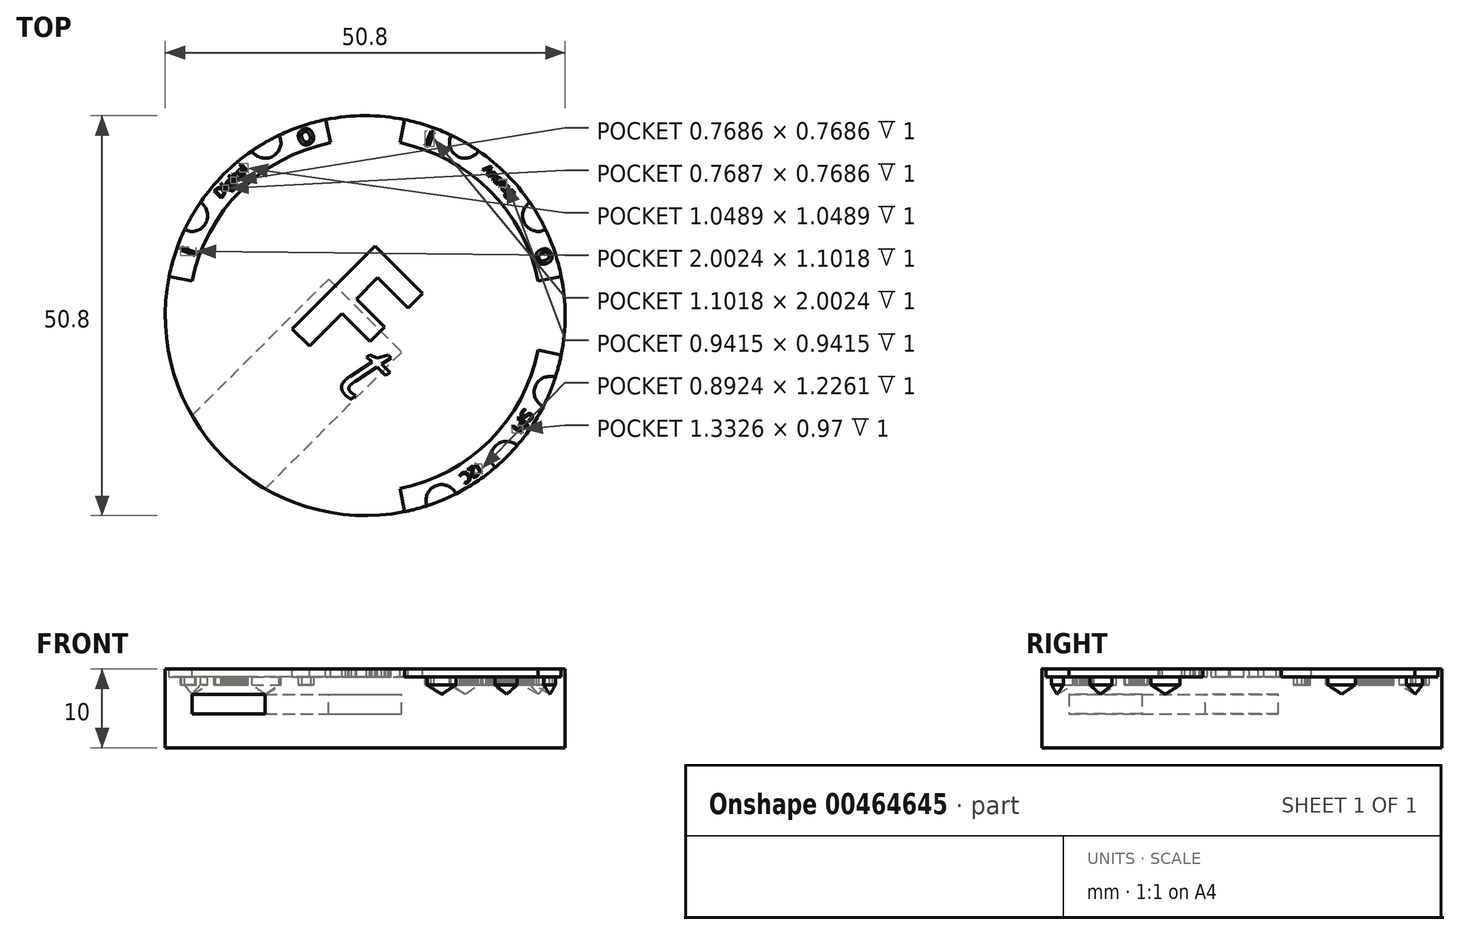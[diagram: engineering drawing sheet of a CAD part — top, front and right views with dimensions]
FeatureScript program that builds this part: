
annotation { "Feature Type Name" : "Feature", "Feature Type Description" : "" }
export const myFeature = defineFeature(function(context is Context, id is Id, definition is map)
    precondition{}
    {
        {
            var Q0;
            Q0=qCreatedBy(makeId("Top.planeOp"),FACE);
            var sketch = newSketch(context, id + "F0", { "sketchPlane" : qUnion([Q0])});
            skCircle(sketch, "E0", {"center": v(0, 0) * mm, "radius": 25.4 * mm});
            skSolve(sketch);
        }
        {
            var Q0;
            Q0=makeQuery(id+"F0.imprint","IMPRINT",FACE,{"disambiguationData":[TD([[makeQuery(id+"F0.imprint","IMPRINT",EDGE,{"derivedFrom":sQuery(id+"F0.wireOp",EDGE,"E0")}),1.0]])]});
            extrude(context, id + "F1", {"entities" : qUnion([Q0]), "depth" : 10 * mm});
        }
        {
            var Q0;
            Q0=makeQuery(id+"F1.opExtrude","CAP_FACE",FACE,{"disambiguationData":[OSD([sQuery(id+"F0.wireOp",EDGE,"E0")])],"isStart":false});
            var sketch = newSketch(context, id + "F2", { "sketchPlane" : qUnion([Q0])});
            skLineSegment(sketch, "E1", {"start": v(0, 0) * mm, "end": v(12.7, 22) * mm});
            skLineSegment(sketch, "E2", {"start": v(0, 0) * mm, "end": v(22, 12.7) * mm});
            skLineSegment(sketch, "E3", {"start": v(0, 25.4) * mm, "end": v(0, -25.4) * mm});
            skLineSegment(sketch, "E4", {"start": v(-25.4, 0) * mm, "end": v(25.4, 0) * mm});
            skLineSegment(sketch, "E5", {"start": v(0, 0) * mm, "end": v(-12.7, 22) * mm});
            skLineSegment(sketch, "E6", {"start": v(0, 0) * mm, "end": v(23.47, -9.72) * mm});
            skLineSegment(sketch, "E7", {"start": v(0, 0) * mm, "end": v(17.96, -17.96) * mm});
            skLineSegment(sketch, "E8", {"start": v(0, 0) * mm, "end": v(9.72, -23.47) * mm});
            skLineSegment(sketch, "E9", {"start": v(0, 0) * mm, "end": v(-17.96, -17.96) * mm});
            skLineSegment(sketch, "E10", {"start": v(0, 0) * mm, "end": v(-22, 12.7) * mm});
            skSolve(sketch);
        }
        {
            var Q0;
            Q0=sQuery(id+"F2.wireOp",VERTEX,"cUKKlthW-F4cE-I2rY-EU5q-HDzWbLOjQpO6.end");
            var Q1;
            Q1=sQuery(id+"F2.wireOp",VERTEX,"E5.end");
            var Q2;
            Q2=sQuery(id+"F2.wireOp",VERTEX,"E1.end");
            var Q3;
            Q3=sQuery(id+"F2.wireOp",VERTEX,"E2.end");
            var Q4;
            Q4=sQuery(id+"F2.wireOp",VERTEX,"E6.end");
            var Q5;
            Q5=sQuery(id+"F2.wireOp",VERTEX,"E7.end");
            var Q6;
            Q6=sQuery(id+"F2.wireOp",VERTEX,"E8.end");
            var Q7;
            Q7=sQuery(id+"F2.wireOp",VERTEX,"E10.end");
            var Q8;
            Q8=makeQuery(id+"F1.opExtrude","SWEPT_BODY",BODY,{"disambiguationData":[OSD([sQuery(id+"F0.wireOp",EDGE,"E0")])]});
            hole(context, id + "F3", {"style" : HoleStyle.SIMPLE, "endStyle" : HoleEndStyle.BLIND, "holeDiameter" : 4 * mm, "holeDepth" : 2 * mm, "isTappedThrough" : true, "tappedDepth" : 12 * mm, "tapClearance" : 3, "locations" : qUnion([Q0, Q1, Q2, Q3, Q4, Q5, Q6, Q7]), "scope" : qUnion([Q8])});
        }
        {
            var Q0;
            Q0=qCreatedBy(makeId("Right.planeOp"),FACE);
            var Q1;
            Q1=sQuery(id+"F2.wireOp",EDGE,"E7");
            cPlane(context, id + "F4", {"entities" : qUnion([Q0, Q1]), "cplaneType" : CPlaneType.LINE_ANGLE, "offset" : 25 * mm, "angle" : 0 * degree, "width" : 150 * mm, "height" : 150 * mm});
        }
        {
            var Q0;
            Q0=qCreatedBy(id+"F4.planeOp",FACE);
            var sketch = newSketch(context, id + "F5", { "sketchPlane" : qUnion([Q0])});
            skLineSegment(sketch, "E11.bottom", {"start": v(-6.57, 4.29) * mm, "end": v(6.57, 4.29) * mm});
            skLineSegment(sketch, "E11.top", {"start": v(-6.57, 6.79) * mm, "end": v(6.57, 6.79) * mm});
            skLineSegment(sketch, "E11.left", {"start": v(-6.57, 4.29) * mm, "end": v(-6.57, 6.79) * mm});
            skLineSegment(sketch, "E11.right", {"start": v(6.57, 4.29) * mm, "end": v(6.57, 6.79) * mm});
            skPoint(sketch, "E11.middle", {"position": v(0, 5.54) * mm});
            skSolve(sketch);
        }
        {
            var Q0;
            Q0=makeQuery(id+"F5.imprint","IMPRINT",FACE,{"disambiguationData":[TD([[makeQuery(id+"F5.imprint","IMPRINT",EDGE,{"derivedFrom":sQuery(id+"F5.wireOp",EDGE,"E11.bottom")}),1.0]])]});
            extrude(context, id + "F6", {"entities" : qUnion([Q0]), "operationType" : NewBodyOperationType.REMOVE, "depth" : 30 * mm});
        }
        {
            var Q0;
            Q0=makeQuery(id+"F1.opExtrude","CAP_FACE",FACE,{"disambiguationData":[OSD([sQuery(id+"F0.wireOp",EDGE,"E0")])],"isStart":false});
            var sketch = newSketch(context, id + "F7", { "sketchPlane" : qUnion([Q0])});
            skText(sketch, "E12", { "text": "F", "fontName": "OpenSans-Bold.ttf"});
            skText(sketch, "E13", { "text": "t", "fontName": "OpenSans-Italic.ttf"});
            skLineSegment(sketch, "E14", {"start": v(0, 0) * mm, "end": v(-17.96, -17.96) * mm});
            skPoint(sketch, "E15", {"position": v(-17.96, -17.96) * mm});
            skLineSegment(sketch, "E16", {"start": v(0, 0) * mm, "end": v(0, -25.4) * mm});
            const initialGuessF7  = {"E12": [-0.0106, -0.00035, 0.7071, -0.7071, 0.015], "E13": [-0.00385, -0.0086, 0.7071, -0.7071, 0.008]};
            skSetInitialGuess(sketch, initialGuessF7);
            skSolve(sketch);
        }
        {
            var Q0;
            Q0=makeQuery(id+"F1.opExtrude","CAP_FACE",FACE,{"disambiguationData":[OSD([sQuery(id+"F0.wireOp",EDGE,"E0")])],"isStart":false});
            var sketch = newSketch(context, id + "F8", { "sketchPlane" : qUnion([Q0])});
            skPoint(sketch, "E17", {"position": v(0, 0) * mm});
            skCircle(sketch, "E18", {"center": v(0, 0) * mm, "radius": 22.4 * mm});
            skLineSegment(sketch, "E19", {"start": v(-25.4, 0) * mm, "end": v(25.4, 0) * mm});
            skLineSegment(sketch, "E20", {"start": v(0, 25.4) * mm, "end": v(0, -25.4) * mm});
            skLineSegment(sketch, "E21", {"start": v(-5, 24.9) * mm, "end": v(-4.4, 21.96) * mm});
            skLineSegment(sketch, "E22", {"start": v(5, 24.9) * mm, "end": v(4.4, 21.96) * mm});
            skLineSegment(sketch, "E23", {"start": v(21.96, 4.4) * mm, "end": v(24.9, 5) * mm});
            skLineSegment(sketch, "E24", {"start": v(21.97, -4.39) * mm, "end": v(24.9, -4.98) * mm});
            skLineSegment(sketch, "E25", {"start": v(4.4, -21.96) * mm, "end": v(5, -24.9) * mm});
            skLineSegment(sketch, "E26", {"start": v(-24.9, 5) * mm, "end": v(-21.96, 4.4) * mm});
            skSolve(sketch);
        }
        {
            var Q0;
            Q0 = qSketchRegion(id + "F7", true);
            extrude(context, id + "F9", {"entities" : qUnion([Q0]), "operationType" : NewBodyOperationType.REMOVE, "oppositeDirection" : true, "depth" : 1 * mm});
        }
        {
            var Q0;
            {var subQ11=sQuery(id+"F8.wireOp",EDGE,"E21");Q0=makeQuery(id+"F8.imprint","IMPRINT",FACE,{"disambiguationData":[TD([[makeQuery(id+"F8.imprint","IMPRINT",EDGE,{"derivedFrom":subQ11}),-1.0]])]});}
            var Q1;
            {var subQ5=sQuery(id+"F8.wireOp",EDGE,"E22");Q1=makeQuery(id+"F8.imprint","IMPRINT",FACE,{"disambiguationData":[TD([[makeQuery(id+"F8.imprint","IMPRINT",EDGE,{"derivedFrom":subQ5}),1.0]])]});}
            var Q2;
            {var subQ1=sQuery(id+"F8.wireOp",EDGE,"E24");Q2=makeQuery(id+"F8.imprint","IMPRINT",FACE,{"disambiguationData":[TD([[makeQuery(id+"F8.imprint","IMPRINT",EDGE,{"derivedFrom":subQ1}),-1.0]])]});}
            extrude(context, id + "F10", {"entities" : qUnion([Q0, Q1, Q2]), "operationType" : NewBodyOperationType.REMOVE, "oppositeDirection" : true, "depth" : 1 * mm});
        }
        {
            var Q0;
            Q0=makeQuery(id+"F10.boolean.opBoolean","COPY",FACE,{"derivedFrom":makeQuery(id+"F10.opExtrude","CAP_FACE",FACE,{"disambiguationData":[OSD([sQuery(id+"F0.wireOp",EDGE,"E0"),sQuery(id+"F3.hole-0.sketch.wireOp",EDGE,"core_line_2"),sQuery(id+"F3.hole-0.sketch.wireOp",EDGE,"core_line_3"),sQuery(id+"F3.hole-6.sketch.wireOp",EDGE,"core_line_2"),sQuery(id+"F3.hole-6.sketch.wireOp",EDGE,"core_line_3"),sQuery(id+"F8.wireOp",EDGE,"E18"),sQuery(id+"F8.wireOp",EDGE,"E21"),sQuery(id+"F8.wireOp",EDGE,"E26")])],"isStart":false})});
            var sketch = newSketch(context, id + "F11", { "sketchPlane" : qUnion([Q0])});
            skPoint(sketch, "E27", {"position": v(-19.34, 15.69) * mm});
            skPoint(sketch, "E28", {"position": v(-23.25, 8.9) * mm});
            skText(sketch, "E29", { "text": "I", "fontName": "OpenSans-Bold.ttf"});
            skPoint(sketch, "E30", {"position": v(-8.9, 23.25) * mm});
            skText(sketch, "E31", { "text": "O", "fontName": "OpenSans-Bold.ttf"});
            skText(sketch, "E32", { "text": "Digital\n", "fontName": "OpenSans-Regular.ttf"});
            skPoint(sketch, "E33", {"position": v(-15.69, 19.34) * mm});
            const initialGuessF11  = {"E29": [-0.0217, 0.0074, 0.35754, 0.9339, 0.002], "E31": [-0.00819, 0.02139, 0.9339, 0.35754, 0.002], "E32": [-0.01844, 0.01479, 0.7071, 0.7071, 0.00127]};
            skSetInitialGuess(sketch, initialGuessF11);
            skSolve(sketch);
        }
        {
            var Q0;
            Q0=makeQuery(id+"F10.boolean.opBoolean","COPY",FACE,{"derivedFrom":makeQuery(id+"F10.opExtrude","CAP_FACE",FACE,{"disambiguationData":[OSD([sQuery(id+"F0.wireOp",EDGE,"E0"),sQuery(id+"F3.hole-1.sketch.wireOp",EDGE,"core_line_2"),sQuery(id+"F3.hole-1.sketch.wireOp",EDGE,"core_line_3"),sQuery(id+"F3.hole-2.sketch.wireOp",EDGE,"core_line_2"),sQuery(id+"F3.hole-2.sketch.wireOp",EDGE,"core_line_3"),sQuery(id+"F8.wireOp",EDGE,"E18"),sQuery(id+"F8.wireOp",EDGE,"E22"),sQuery(id+"F8.wireOp",EDGE,"E23")])],"isStart":false})});
            var sketch = newSketch(context, id + "F12", { "sketchPlane" : qUnion([Q0])});
            skPoint(sketch, "E34", {"position": v(8.9, 23.25) * mm});
            skPoint(sketch, "E35", {"position": v(15.69, 19.34) * mm});
            skPoint(sketch, "E36", {"position": v(19.34, 15.69) * mm});
            skPoint(sketch, "E37", {"position": v(23.25, 8.9) * mm});
            skText(sketch, "E38", { "text": "I", "fontName": "OpenSans-Bold.ttf"});
            skText(sketch, "E39", { "text": "O", "fontName": "OpenSans-Bold.ttf"});
            skText(sketch, "E40", { "text": "Analog", "fontName": "OpenSans-Regular.ttf"});
            const initialGuessF12  = {"E38": [0.0074, 0.0217, 0.9339, -0.35754, 0.002], "E39": [0.02139, 0.00819, 0.35754, -0.9339, 0.002], "E40": [0.01488, 0.01853, 0.7071, -0.7071, 0.00114]};
            skSetInitialGuess(sketch, initialGuessF12);
            skSolve(sketch);
        }
        {
            var Q0;
            Q0=makeQuery(id+"F10.boolean.opBoolean","COPY",FACE,{"derivedFrom":makeQuery(id+"F10.opExtrude","CAP_FACE",FACE,{"disambiguationData":[OSD([sQuery(id+"F0.wireOp",EDGE,"E0"),sQuery(id+"F3.hole-3.sketch.wireOp",EDGE,"core_line_2"),sQuery(id+"F3.hole-3.sketch.wireOp",EDGE,"core_line_3"),sQuery(id+"F3.hole-4.sketch.wireOp",EDGE,"core_line_2"),sQuery(id+"F3.hole-4.sketch.wireOp",EDGE,"core_line_3"),sQuery(id+"F3.hole-5.sketch.wireOp",EDGE,"core_line_2"),sQuery(id+"F3.hole-5.sketch.wireOp",EDGE,"core_line_3"),sQuery(id+"F8.wireOp",EDGE,"E18"),sQuery(id+"F8.wireOp",EDGE,"E24"),sQuery(id+"F8.wireOp",EDGE,"E25")])],"isStart":false})});
            var sketch = newSketch(context, id + "F13", { "sketchPlane" : qUnion([Q0])});
            skPoint(sketch, "E41", {"position": v(21.48, -12.6) * mm});
            skPoint(sketch, "E42", {"position": v(19.86, -15.02) * mm});
            skPoint(sketch, "E43", {"position": v(15.02, -19.86) * mm});
            skPoint(sketch, "E44", {"position": v(12.6, -21.48) * mm});
            skText(sketch, "E45", { "text": "SPI", "fontName": "OpenSans-Regular.ttf"});
            skText(sketch, "E46", { "text": "I2C\n", "fontName": "OpenSans-Regular.ttf"});
            const initialGuessF13  = {"E45": [0.02023, -0.01177, -0.55557, -0.83147, 0.0015], "E46": [0.01425, -0.01871, -0.83147, -0.55557, 0.00138]};
            skSetInitialGuess(sketch, initialGuessF13);
            skSolve(sketch);
        }
        {
            var Q0;
            Q0 = qSketchRegion(id + "F11", true);
            var Q1;
            Q1 = qSketchRegion(id + "F12", true);
            var Q2;
            Q2 = qSketchRegion(id + "F13", true);
            extrude(context, id + "F14", {"entities" : qUnion([Q0, Q1, Q2]), "operationType" : NewBodyOperationType.REMOVE, "oppositeDirection" : true, "depth" : 1 * mm});
        }
    });
